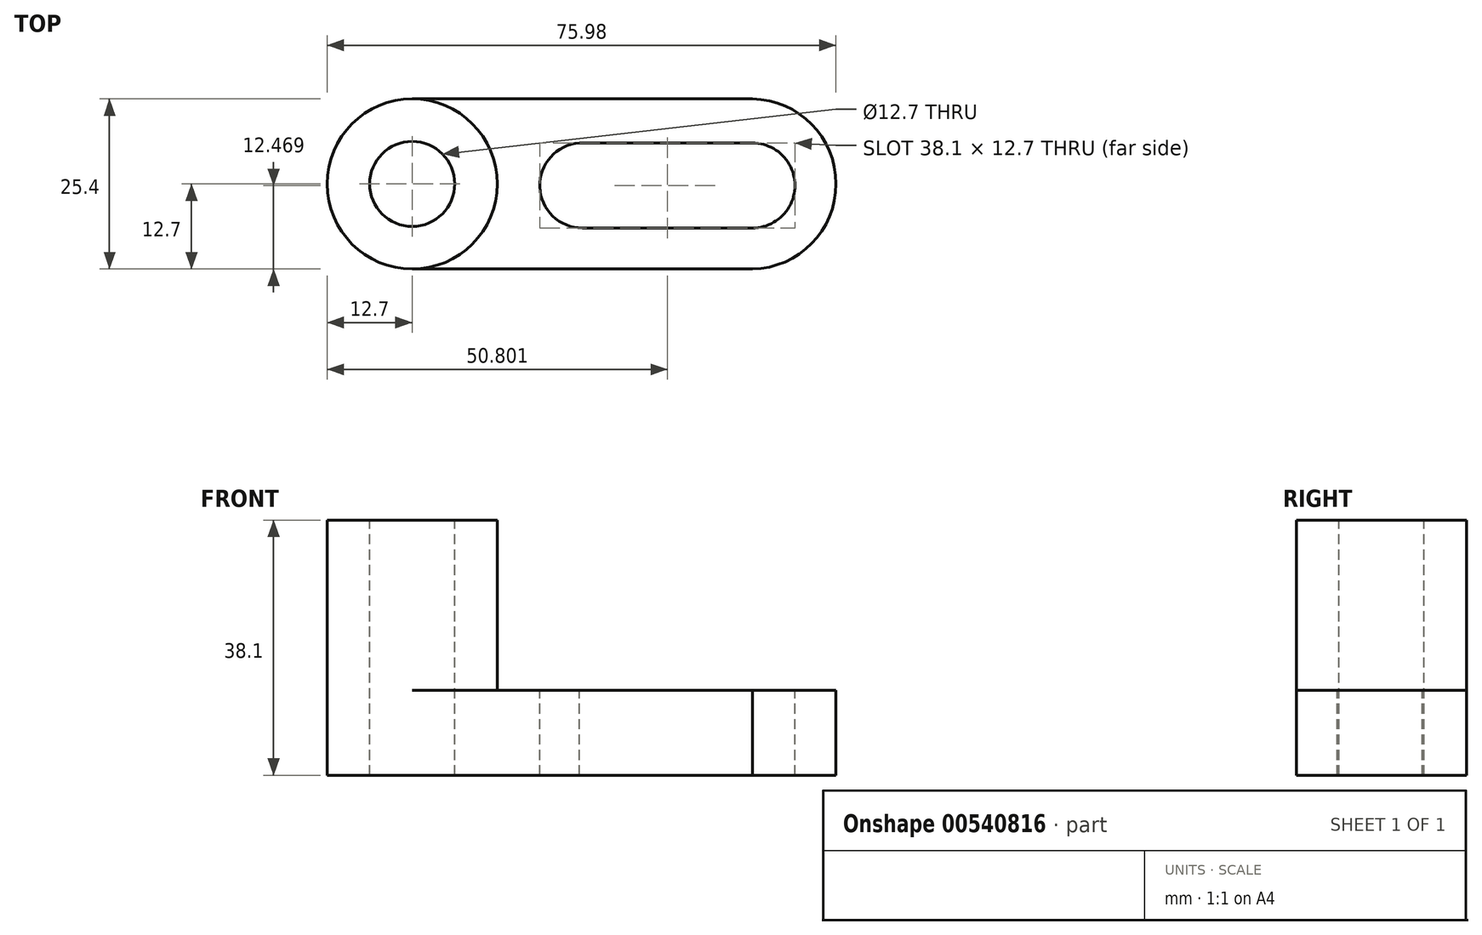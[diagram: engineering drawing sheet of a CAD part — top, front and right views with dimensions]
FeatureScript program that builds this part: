
annotation { "Feature Type Name" : "Feature", "Feature Type Description" : "" }
export const myFeature = defineFeature(function(context is Context, id is Id, definition is map)
    precondition{}
    {
        {
            var Q0;
            Q0=qCreatedBy(makeId("Front.planeOp"),FACE);
            var sketch = newSketch(context, id + "F0", { "sketchPlane" : qUnion([Q0])});
            skLineSegment(sketch, "E0", {"start": v(0, 0) * mm, "end": v(0, 38.1) * mm});
            skLineSegment(sketch, "E1", {"start": v(0, 38.1) * mm, "end": v(25.4, 38.1) * mm});
            skLineSegment(sketch, "E2", {"start": v(25.4, 38.1) * mm, "end": v(25.4, 12.7) * mm});
            skLineSegment(sketch, "E3", {"start": v(25.4, 12.7) * mm, "end": v(76.2, 12.7) * mm});
            skLineSegment(sketch, "E4", {"start": v(76.2, 12.7) * mm, "end": v(76.2, 0) * mm});
            skLineSegment(sketch, "E5", {"start": v(76.2, 0) * mm, "end": v(0, 0) * mm});
            skSolve(sketch);
        }
        {
            var Q0;
            Q0=makeQuery(id+"F0.imprint","IMPRINT",FACE,{"disambiguationData":[TD([[makeQuery(id+"F0.imprint","IMPRINT",EDGE,{"derivedFrom":sQuery(id+"F0.wireOp",EDGE,"E0")}),-1.0]])]});
            extrude(context, id + "F1", {"entities" : qUnion([Q0]), "depth" : 25.4 * mm, "offsetDistance" : 25.4 * mm});
        }
        {
            var Q0;
            Q0=makeQuery(id+"F1.opExtrude","SWEPT_FACE",FACE,{"disambiguationData":[OSD([sQuery(id+"F0.wireOp",EDGE,"E1")])]});
            var sketch = newSketch(context, id + "F2", { "sketchPlane" : qUnion([Q0])});
            skCircle(sketch, "E6", {"center": v(12.7, -12.7) * mm, "radius": 12.7 * mm});
            skCircle(sketch, "E7", {"center": v(12.7, -12.7) * mm, "radius": 6.35 * mm});
            skSolve(sketch);
        }
        {
            var Q0;
            {var subQ1=sQuery(id+"F0.wireOp",EDGE,"E1");var subQ6=makeQuery(id+"F1.opExtrude","CAP_EDGE",EDGE,{"disambiguationData":[OSD([subQ1])],"isStart":false});Q0=makeQuery(id+"F2.imprint","IMPRINT",FACE,{"disambiguationData":[TD([[makeQuery(id+"F2.imprint","IMPRINT",EDGE,{"derivedFrom":subQ6}),1.0]])]});}
            var Q1;
            {var subQ1=sQuery(id+"F0.wireOp",EDGE,"E1");var subQ6=makeQuery(id+"F1.opExtrude","CAP_EDGE",EDGE,{"disambiguationData":[OSD([subQ1])],"isStart":true});Q1=makeQuery(id+"F2.imprint","IMPRINT",FACE,{"disambiguationData":[TD([[makeQuery(id+"F2.imprint","IMPRINT",EDGE,{"derivedFrom":subQ6}),-1.0]])]});}
            var Q2;
            Q2=makeQuery(id+"F2.imprint","IMPRINT",FACE,{"disambiguationData":[TD([[makeQuery(id+"F2.imprint","IMPRINT",EDGE,{"derivedFrom":sQuery(id+"F2.wireOp",EDGE,"E7")}),1.0]])]});
            extrude(context, id + "F3", {"entities" : qUnion([Q0, Q1, Q2]), "operationType" : NewBodyOperationType.REMOVE, "oppositeDirection" : true, "depth" : 25.4 * mm, "offsetDistance" : 25.4 * mm});
        }
        {
            var Q0;
            {var subQ0=sQuery(id+"F0.wireOp",EDGE,"E1");var subQ1=makeQuery(id+"F1.opExtrude","CAP_EDGE",EDGE,{"disambiguationData":[OSD([subQ0])],"isStart":false});var subQ2=sQuery(id+"F0.wireOp",EDGE,"E2");var subQ3=makeQuery(id+"F1.opExtrude","SWEPT_EDGE",EDGE,{"disambiguationData":[OSD([subQ0,subQ2])]});var subQ4=makeQuery(id+"F2.imprint","INTERSECT",VERTEX,{"derivedFrom":[subQ3,subQ1]});var subQ5=sQuery(id+"F2.wireOp",EDGE,"E6");var subQ6=makeQuery(id+"F2.imprint","INTERSECT",VERTEX,{"derivedFrom":[subQ1,subQ5]});var subQ8=makeQuery(id+"F1.opExtrude","CAP_EDGE",EDGE,{"disambiguationData":[OSD([subQ0])],"isStart":true});var subQ9=makeQuery(id+"F2.imprint","INTERSECT",VERTEX,{"derivedFrom":[subQ3,subQ8]});var subQ10=makeQuery(id+"F2.imprint","INTERSECT",VERTEX,{"derivedFrom":[subQ8,subQ5]});Q0=makeQuery(id+"F3.boolean.opBoolean","MERGE",FACE,{"derivedFrom":[makeQuery(id+"F1.opExtrude","SWEPT_FACE",FACE,{"disambiguationData":[OSD([sQuery(id+"F0.wireOp",EDGE,"E3")])]}),makeQuery(id+"F3.opExtrude","CAP_FACE",FACE,{"disambiguationData":[OSD([subQ0,subQ2,subQ5]),TDD([makeQuery(id+"F2.imprint","IMPRINT",EDGE,{"disambiguationData":[TD([[subQ10,1.0]])],"derivedFrom":subQ5}),makeQuery(id+"F2.imprint","IMPRINT",EDGE,{"disambiguationData":[TD([[subQ9,1.0]])],"derivedFrom":subQ3}),makeQuery(id+"F2.imprint","IMPRINT",EDGE,{"disambiguationData":[TD([[subQ10,-1.0]])],"derivedFrom":subQ8})])],"isStart":false}),makeQuery(id+"F3.opExtrude","CAP_FACE",FACE,{"disambiguationData":[OSD([subQ0,subQ2,subQ5]),TDD([makeQuery(id+"F2.imprint","IMPRINT",EDGE,{"disambiguationData":[TD([[subQ6,-1.0]])],"derivedFrom":subQ5}),makeQuery(id+"F2.imprint","IMPRINT",EDGE,{"disambiguationData":[TD([[subQ4,-1.0]])],"derivedFrom":subQ3}),makeQuery(id+"F2.imprint","IMPRINT",EDGE,{"disambiguationData":[TD([[subQ6,-1.0]])],"derivedFrom":subQ1})])],"isStart":false})]});}
            var sketch = newSketch(context, id + "F4", { "sketchPlane" : qUnion([Q0])});
            skCircle(sketch, "E8", {"center": v(38.1, -12.93) * mm, "radius": 6.35 * mm});
            skCircle(sketch, "E9", {"center": v(63.5, -12.93) * mm, "radius": 6.35 * mm});
            skLineSegment(sketch, "E10", {"start": v(37.67, -6.6) * mm, "end": v(63.5, -6.58) * mm});
            skLineSegment(sketch, "E11", {"start": v(63.5, -6.58) * mm, "end": v(63.5, -19.28) * mm});
            skLineSegment(sketch, "E12", {"start": v(63.5, -19.28) * mm, "end": v(38.1, -19.28) * mm});
            skLineSegment(sketch, "E13", {"start": v(38.1, -19.28) * mm, "end": v(37.67, -6.6) * mm});
            skArc(sketch, "E14", {"start": v(63.5, -25.4) * mm, "mid": v(75.98, -12.7) * mm, "end": v(63.5, 0) * mm});
            skSolve(sketch);
        }
        {
            var Q0;
            {var subQ0=sQuery(id+"F0.wireOp",EDGE,"E1");var subQ1=makeQuery(id+"F1.opExtrude","CAP_EDGE",EDGE,{"disambiguationData":[OSD([subQ0])],"isStart":true});var subQ2=sQuery(id+"F0.wireOp",EDGE,"E0");var subQ3=makeQuery(id+"F1.opExtrude","SWEPT_EDGE",EDGE,{"disambiguationData":[OSD([subQ2,subQ0])]});var subQ4=makeQuery(id+"F2.imprint","INTERSECT",VERTEX,{"derivedFrom":[subQ3,subQ1]});var subQ5=sQuery(id+"F2.wireOp",EDGE,"E6");var subQ6=makeQuery(id+"F2.imprint","INTERSECT",VERTEX,{"derivedFrom":[subQ1,subQ5]});Q0=makeQuery(id+"F3.boolean.opBoolean","COPY",FACE,{"derivedFrom":makeQuery(id+"F3.opExtrude","CAP_FACE",FACE,{"disambiguationData":[OSD([subQ2,subQ0,subQ5]),TDD([makeQuery(id+"F2.imprint","IMPRINT",EDGE,{"disambiguationData":[TD([[subQ6,-1.0]])],"derivedFrom":subQ5}),makeQuery(id+"F2.imprint","IMPRINT",EDGE,{"disambiguationData":[TD([[subQ4,1.0]])],"derivedFrom":subQ3}),makeQuery(id+"F2.imprint","IMPRINT",EDGE,{"disambiguationData":[TD([[subQ6,1.0]])],"derivedFrom":subQ1})])],"isStart":false})});}
            var Q1;
            {var subQ0=sQuery(id+"F0.wireOp",EDGE,"E1");var subQ1=makeQuery(id+"F1.opExtrude","CAP_EDGE",EDGE,{"disambiguationData":[OSD([subQ0])],"isStart":false});var subQ2=sQuery(id+"F0.wireOp",EDGE,"E0");var subQ3=makeQuery(id+"F1.opExtrude","SWEPT_EDGE",EDGE,{"disambiguationData":[OSD([subQ2,subQ0])]});var subQ4=makeQuery(id+"F2.imprint","INTERSECT",VERTEX,{"derivedFrom":[subQ3,subQ1]});var subQ5=sQuery(id+"F2.wireOp",EDGE,"E6");var subQ6=makeQuery(id+"F2.imprint","INTERSECT",VERTEX,{"derivedFrom":[subQ1,subQ5]});Q1=makeQuery(id+"F3.boolean.opBoolean","COPY",FACE,{"derivedFrom":makeQuery(id+"F3.opExtrude","CAP_FACE",FACE,{"disambiguationData":[OSD([subQ2,subQ0,subQ5]),TDD([makeQuery(id+"F2.imprint","IMPRINT",EDGE,{"disambiguationData":[TD([[subQ6,1.0]])],"derivedFrom":subQ5}),makeQuery(id+"F2.imprint","IMPRINT",EDGE,{"disambiguationData":[TD([[subQ4,-1.0]])],"derivedFrom":subQ3}),makeQuery(id+"F2.imprint","IMPRINT",EDGE,{"disambiguationData":[TD([[subQ6,1.0]])],"derivedFrom":subQ1})])],"isStart":false})});}
            var Q2;
            Q2=makeQuery(id+"F3.boolean.opBoolean","COPY",FACE,{"derivedFrom":makeQuery(id+"F3.opExtrude","CAP_FACE",FACE,{"disambiguationData":[OSD([sQuery(id+"F2.wireOp",EDGE,"E7")])],"isStart":false})});
            extrude(context, id + "F5", {"entities" : qUnion([Q0, Q1, Q2]), "operationType" : NewBodyOperationType.REMOVE, "oppositeDirection" : true, "depth" : 25.4 * mm, "offsetDistance" : 25.4 * mm});
        }
        {
            var Q0;
            {var subQ0=sQuery(id+"F4.wireOp",EDGE,"E13");Q0=makeQuery(id+"F4.imprint","IMPRINT",FACE,{"disambiguationData":[TD([[makeQuery(id+"F4.imprint","IMPRINT",EDGE,{"derivedFrom":subQ0}),-1.0]])]});}
            var Q1;
            {var subQ0=sQuery(id+"F4.wireOp",EDGE,"E13");Q1=makeQuery(id+"F4.imprint","IMPRINT",FACE,{"disambiguationData":[TD([[makeQuery(id+"F4.imprint","IMPRINT",EDGE,{"derivedFrom":subQ0}),1.0]])]});}
            var Q2;
            {var subQ0=sQuery(id+"F4.wireOp",EDGE,"E12");Q2=makeQuery(id+"F4.imprint","IMPRINT",FACE,{"disambiguationData":[TD([[makeQuery(id+"F4.imprint","IMPRINT",EDGE,{"derivedFrom":subQ0}),-1.0]])]});}
            var Q3;
            {var subQ0=sQuery(id+"F4.wireOp",EDGE,"E11");Q3=makeQuery(id+"F4.imprint","IMPRINT",FACE,{"disambiguationData":[TD([[makeQuery(id+"F4.imprint","IMPRINT",EDGE,{"derivedFrom":subQ0}),-1.0]])]});}
            var Q4;
            {var subQ0=sQuery(id+"F4.wireOp",EDGE,"E11");Q4=makeQuery(id+"F4.imprint","IMPRINT",FACE,{"disambiguationData":[TD([[makeQuery(id+"F4.imprint","IMPRINT",EDGE,{"derivedFrom":subQ0}),1.0]])]});}
            var Q5;
            {var subQ0=sQuery(id+"F4.wireOp",EDGE,"E14");Q5=makeQuery(id+"F4.imprint","IMPRINT",FACE,{"disambiguationData":[TD([[makeQuery(id+"F4.imprint","IMPRINT",EDGE,{"derivedFrom":subQ0}),-1.0]])]});}
            extrude(context, id + "F6", {"entities" : qUnion([Q0, Q1, Q2, Q3, Q4, Q5]), "operationType" : NewBodyOperationType.REMOVE, "oppositeDirection" : true, "depth" : 25.4 * mm, "offsetDistance" : 25.4 * mm});
        }
    });
